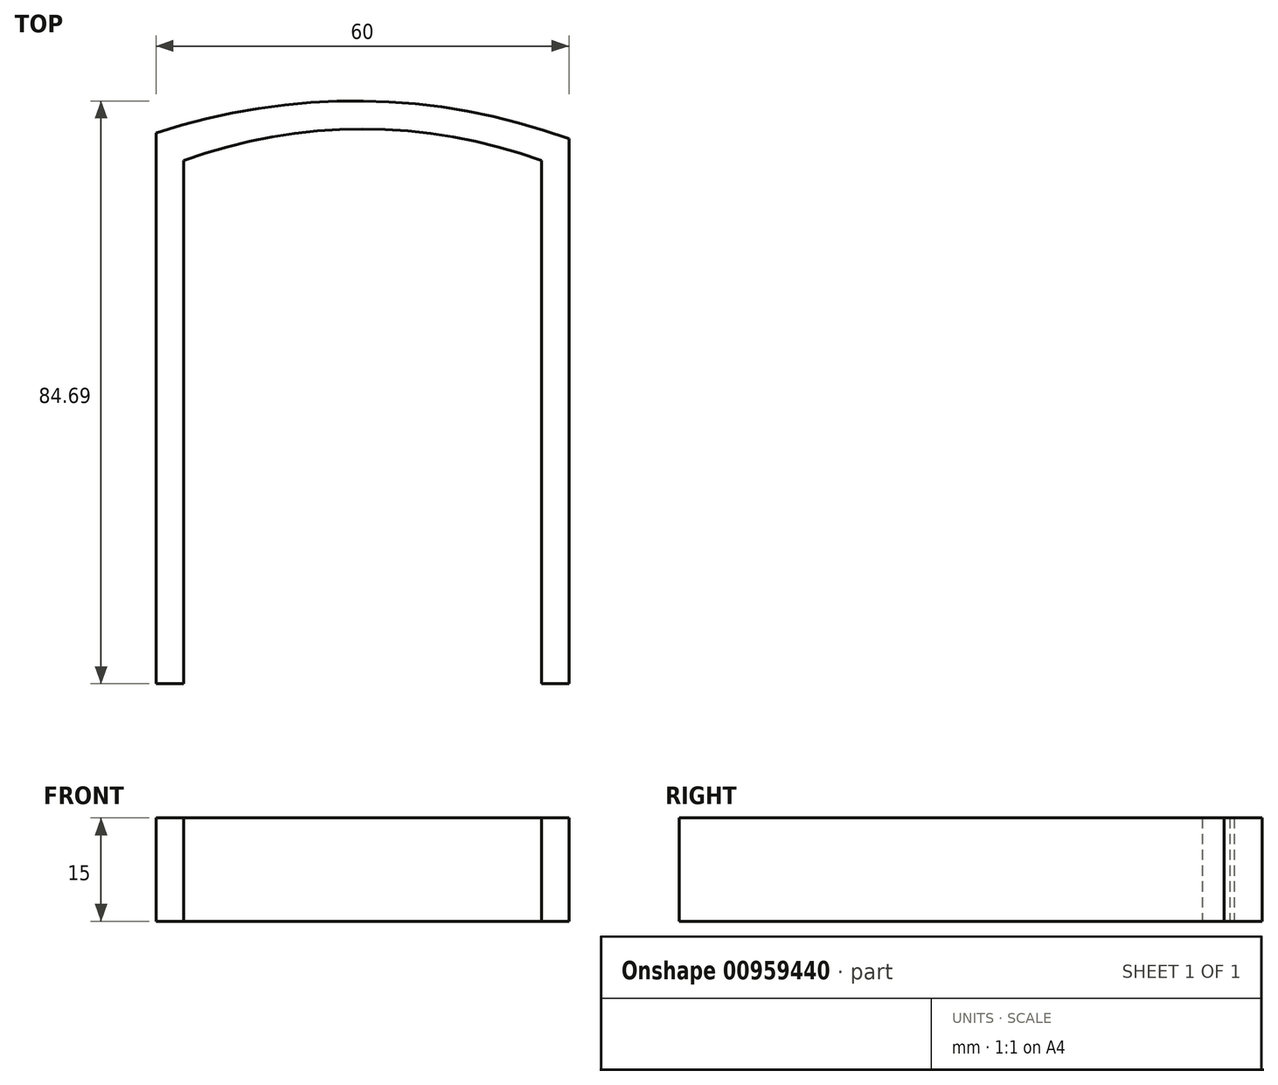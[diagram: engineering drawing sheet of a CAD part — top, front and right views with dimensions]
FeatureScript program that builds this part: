
annotation { "Feature Type Name" : "Feature", "Feature Type Description" : "" }
export const myFeature = defineFeature(function(context is Context, id is Id, definition is map)
    precondition{}
    {
        {
            var Q0;
            Q0=qCreatedBy(makeId("Top.planeOp"),FACE);
            var sketch = newSketch(context, id + "F0", { "sketchPlane" : qUnion([Q0])});
            skLineSegment(sketch, "E0.bottom", {"start": v(-36.96, -30.17) * mm, "end": v(-32.96, -30.17) * mm});
            skLineSegment(sketch, "E0.left", {"start": v(-36.96, -30.17) * mm, "end": v(-36.96, 49.83) * mm});
            skLineSegment(sketch, "E0.right", {"start": v(23.04, -30.17) * mm, "end": v(23.04, 49.02) * mm});
            skLineSegment(sketch, "E1", {"start": v(-32.96, -30.17) * mm, "end": v(-32.96, 45.83) * mm});
            skLineSegment(sketch, "E2", {"start": v(19.04, 45.83) * mm, "end": v(19.04, -30.17) * mm});
            skArc(sketch, "E3", {"start": v(23.04, 49.02) * mm, "mid": v(-6.89, 54.51) * mm, "end": v(-36.96, 49.83) * mm});
            skArc(sketch, "E4", {"start": v(19.04, 45.83) * mm, "mid": v(-6.96, 50.46) * mm, "end": v(-32.96, 45.83) * mm});
            skLineSegment(sketch, "E5.trimOffspring", {"start": v(19.04, -30.17) * mm, "end": v(23.04, -30.17) * mm});
            skSolve(sketch);
        }
        {
            var Q0;
            Q0 = qSketchRegion(id + "F0", true);
            extrude(context, id + "F1", {"entities" : qUnion([Q0]), "depth" : 15 * mm, "offsetDistance" : 25 * mm});
        }
    });
